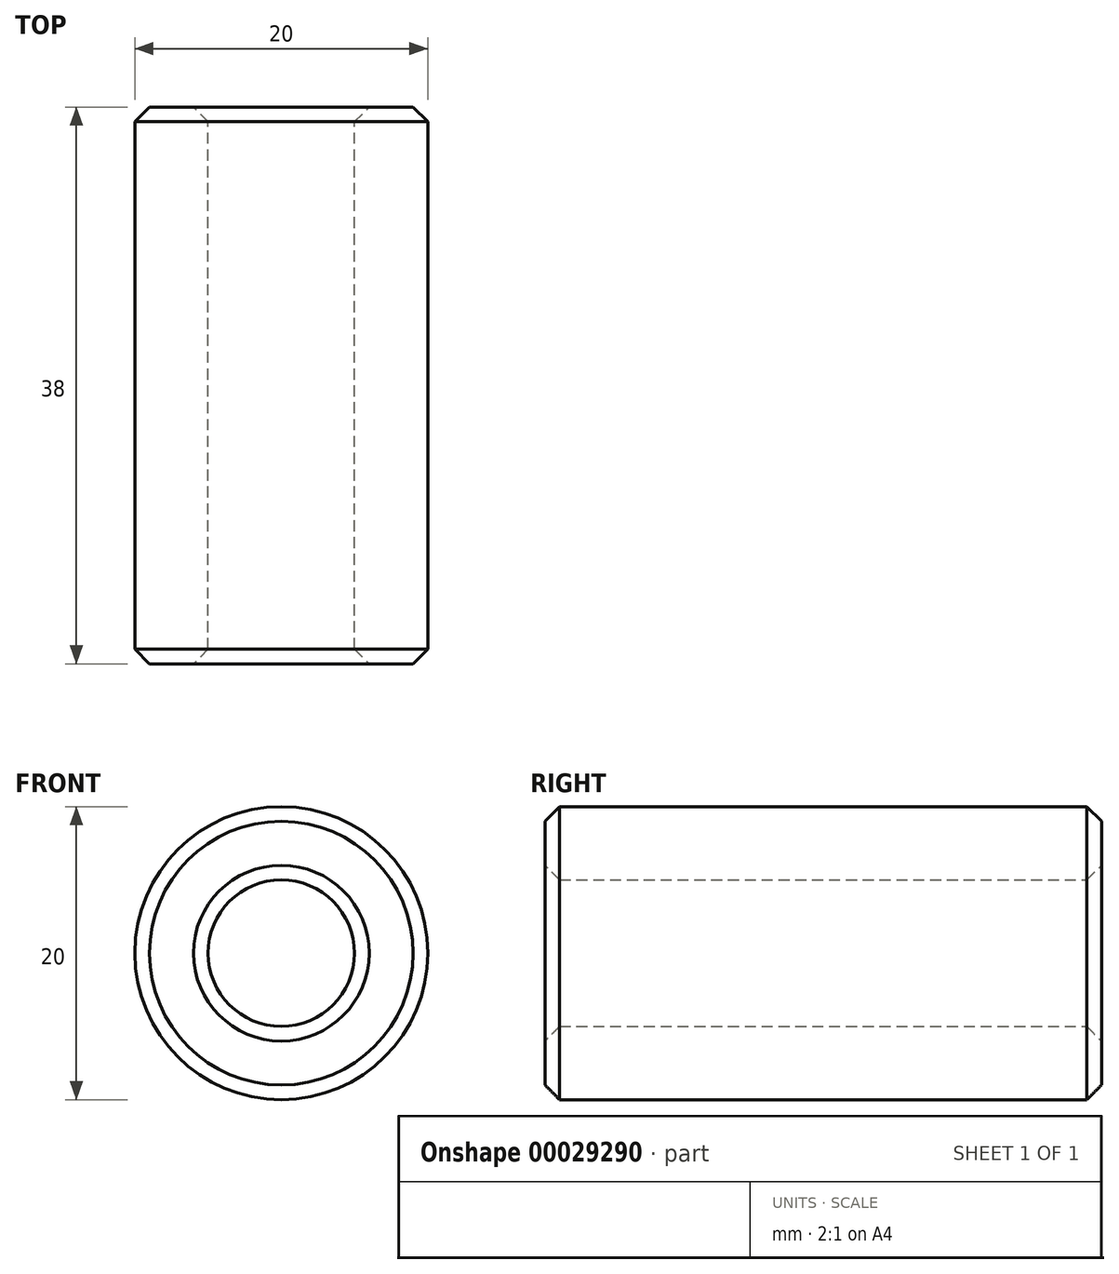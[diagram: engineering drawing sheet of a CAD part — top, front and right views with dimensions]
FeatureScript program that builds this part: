
annotation { "Feature Type Name" : "Feature", "Feature Type Description" : "" }
export const myFeature = defineFeature(function(context is Context, id is Id, definition is map)
    precondition{}
    {
        {
            var Q0;
            Q0=qCreatedBy(makeId("Front.planeOp"),FACE);
            var sketch = newSketch(context, id + "F0", { "sketchPlane" : qUnion([Q0])});
            skCircle(sketch, "E0", {"center": v(0, 0) * mm, "radius": 5 * mm});
            skCircle(sketch, "E1", {"center": v(0, 0) * mm, "radius": 10 * mm});
            skSolve(sketch);
        }
        {
            var Q0;
            Q0 = qSketchRegion(id + "F0", true);
            extrude(context, id + "F1", {"entities" : qUnion([Q0]), "depth" : 38 * mm});
        }
        {
            var Q0;
            Q0=makeQuery(id+"F1.opExtrude","CAP_FACE",FACE,{"disambiguationData":[OSD([sQuery(id+"F0.wireOp",EDGE,"E0"),sQuery(id+"F0.wireOp",EDGE,"E1")])],"isStart":false});
            var Q1;
            Q1=makeQuery(id+"F1.opExtrude","CAP_FACE",FACE,{"disambiguationData":[OSD([sQuery(id+"F0.wireOp",EDGE,"E0"),sQuery(id+"F0.wireOp",EDGE,"E1")])],"isStart":true});
            chamfer(context, id + "F2", {"entities" : qUnion([Q0, Q1]), "width" : 1 * mm, "tangentPropagation" : true});
        }
    });
